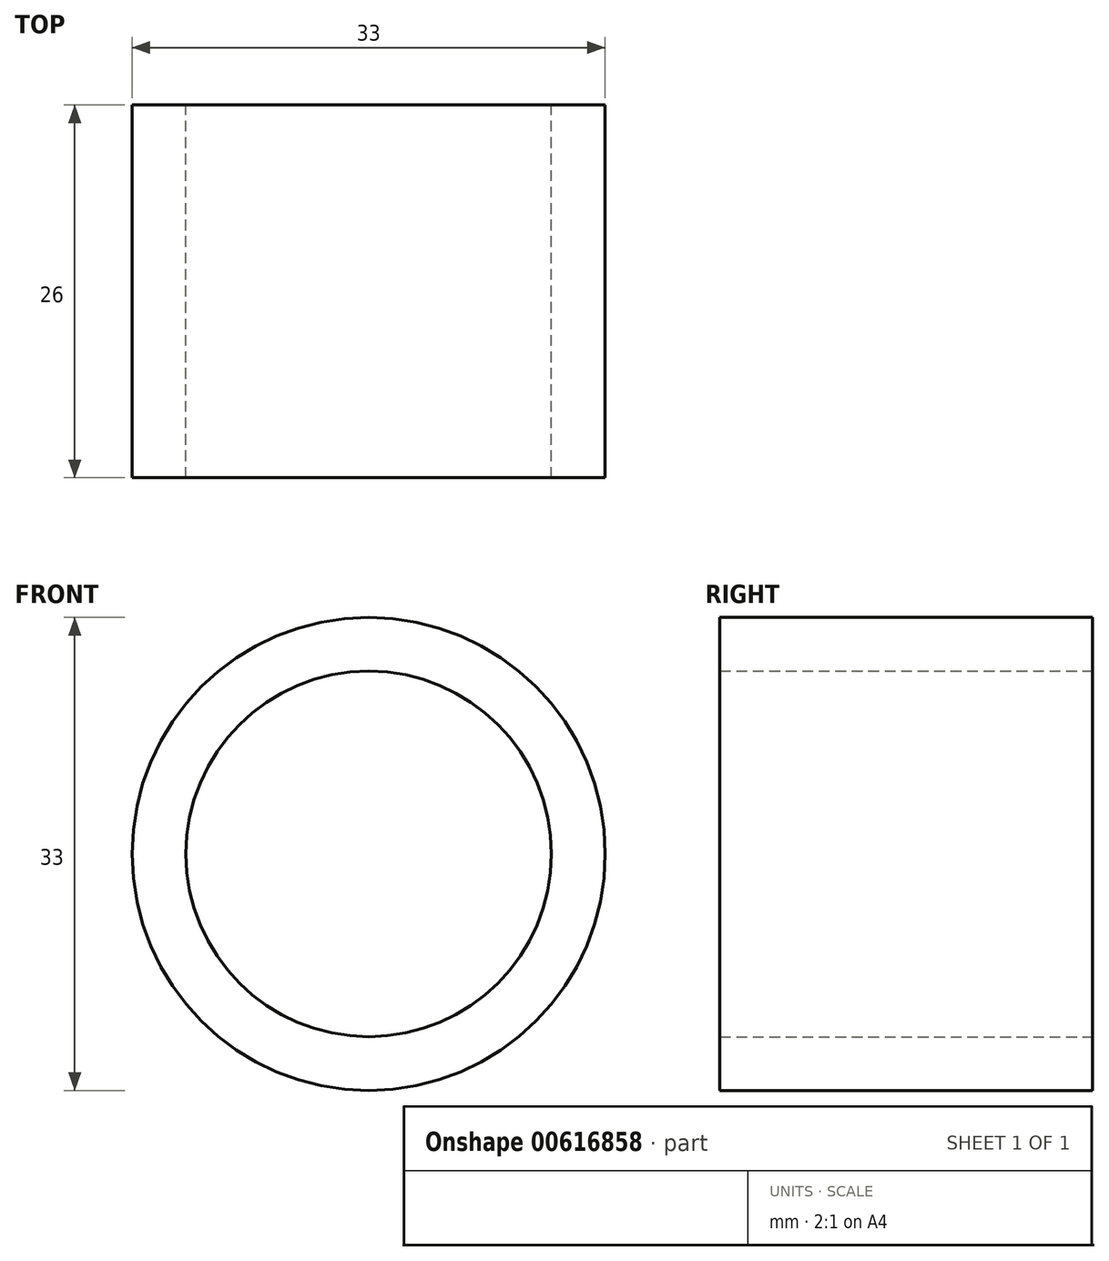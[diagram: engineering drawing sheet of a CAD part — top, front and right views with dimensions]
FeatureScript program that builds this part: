
annotation { "Feature Type Name" : "Feature", "Feature Type Description" : "" }
export const myFeature = defineFeature(function(context is Context, id is Id, definition is map)
    precondition{}
    {
        {
            var Q0;
            Q0=qCreatedBy(makeId("Front.planeOp"),FACE);
            var sketch = newSketch(context, id + "F0", { "sketchPlane" : qUnion([Q0])});
            skCircle(sketch, "E0", {"center": v(0, 0) * mm, "radius": 12.75 * mm});
            skCircle(sketch, "E1", {"center": v(0, 0) * mm, "radius": 16.5 * mm});
            skSolve(sketch);
        }
        {
            var Q0;
            Q0 = qSketchRegion(id + "F0", true);
            extrude(context, id + "F1", {"entities" : qUnion([Q0]), "depth" : 26 * mm, "offsetDistance" : 25 * mm});
        }
    });
